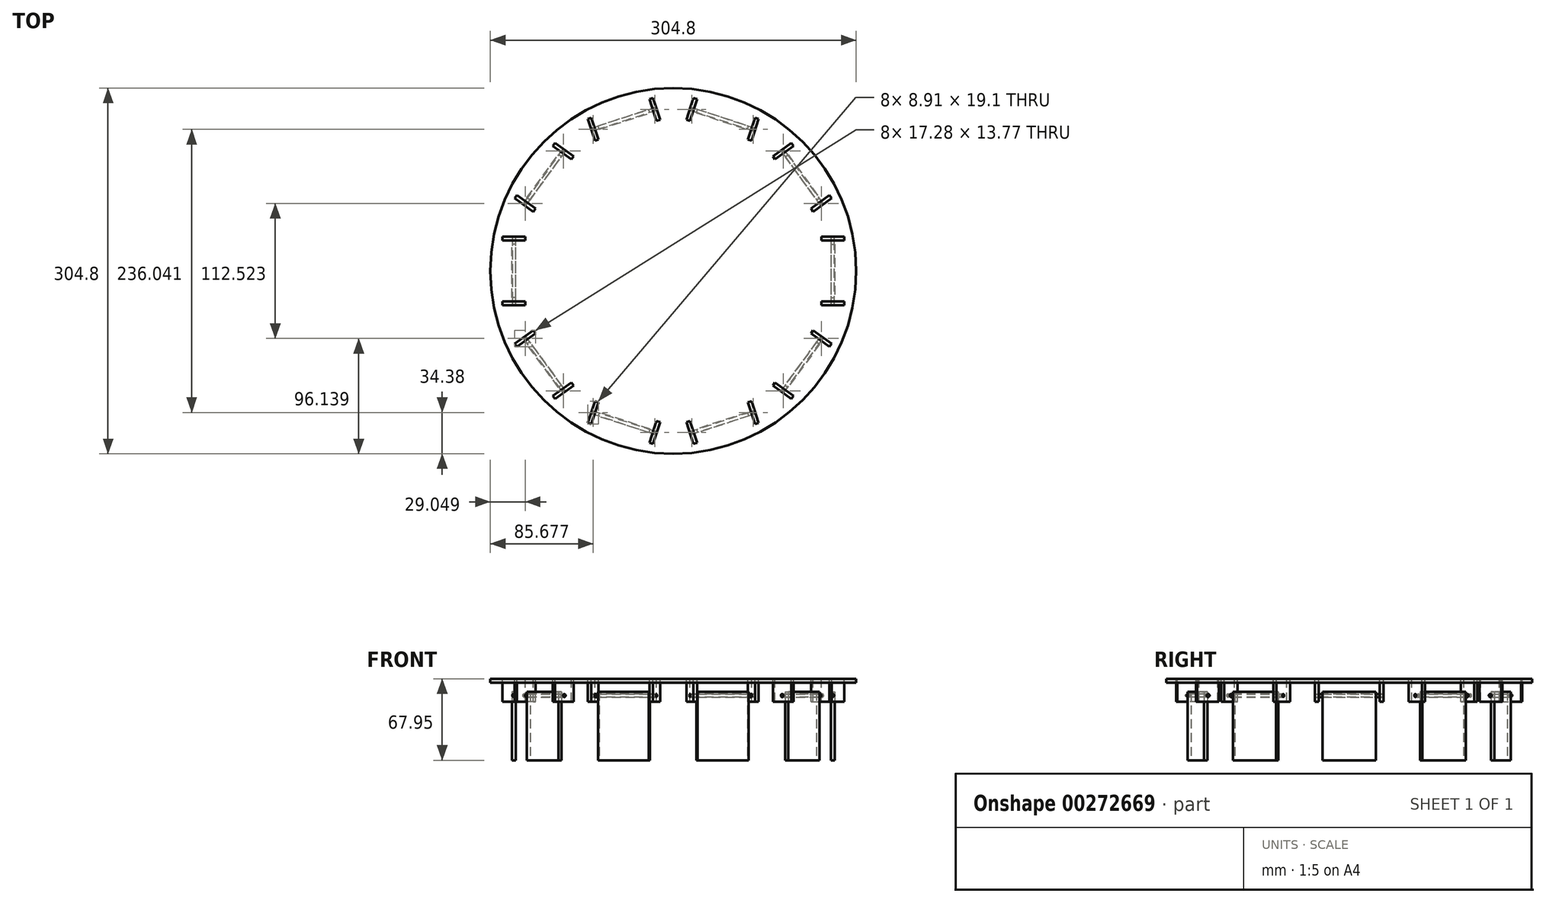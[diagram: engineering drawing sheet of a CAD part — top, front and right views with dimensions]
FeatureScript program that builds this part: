
annotation { "Feature Type Name" : "Feature", "Feature Type Description" : "" }
export const myFeature = defineFeature(function(context is Context, id is Id, definition is map)
    precondition{}
    {
        {
            var Q0;
            Q0=qCreatedBy(makeId("Top.planeOp"),FACE);
            var sketch = newSketch(context, id + "F0", { "sketchPlane" : qUnion([Q0])});
            skCircle(sketch, "E0", {"center": v(0, 0) * mm, "radius": 152.4 * mm});
            skSolve(sketch);
        }
        {
            var Q0;
            Q0 = qSketchRegion(id + "F0", true);
            extrude(context, id + "F1", {"entities" : qUnion([Q0]), "depth" : 3.17 * mm});
        }
        {
            var Q0;
            Q0=makeQuery(id+"F1.opExtrude","CAP_FACE",FACE,{"disambiguationData":[OSD([sQuery(id+"F0.wireOp",EDGE,"E0")])],"isStart":false});
            var sketch = newSketch(context, id + "F2", { "sketchPlane" : qUnion([Q0])});
            skLineSegment(sketch, "E1", {"start": v(0, 0) * mm, "end": v(0, 152.4) * mm, "construction": true});
            skLineSegment(sketch, "E2.1.0", {"start": v(0, 0) * mm, "end": v(-89.58, 123.3) * mm, "construction": true});
            skLineSegment(sketch, "E2.2.0", {"start": v(0, 0) * mm, "end": v(-144.94, 47.1) * mm, "construction": true});
            skLineSegment(sketch, "E2.3.0", {"start": v(0, 0) * mm, "end": v(-144.94, -47.1) * mm, "construction": true});
            skLineSegment(sketch, "E2.4.0", {"start": v(0, 0) * mm, "end": v(-89.58, -123.3) * mm, "construction": true});
            skLineSegment(sketch, "E2.5.0", {"start": v(0, 0) * mm, "end": v(0, -152.4) * mm, "construction": true});
            skLineSegment(sketch, "E2.6.0", {"start": v(0, 0) * mm, "end": v(89.58, -123.3) * mm, "construction": true});
            skLineSegment(sketch, "E2.7.0", {"start": v(0, 0) * mm, "end": v(144.94, -47.1) * mm, "construction": true});
            skLineSegment(sketch, "E2.8.0", {"start": v(0, 0) * mm, "end": v(144.94, 47.1) * mm, "construction": true});
            skLineSegment(sketch, "E2.9.0", {"start": v(0, 0) * mm, "end": v(89.58, 123.3) * mm, "construction": true});
            skPoint(sketch, "E2.center", {"position": v(0, 0) * mm});
            skLineSegment(sketch, "E3", {"start": v(0, 139.7) * mm, "end": v(82.11, 113.02) * mm, "construction": true});
            skLineSegment(sketch, "E4", {"start": v(16.23, 134.43) * mm, "end": v(66.72, 118.02) * mm, "construction": true});
            skLineSegment(sketch, "E5", {"start": v(41.06, 126.36) * mm, "end": v(0, 0) * mm, "construction": true});
            skLineSegment(sketch, "E6.bottom", {"start": v(65.29, 108.47) * mm, "end": v(62.27, 109.45) * mm});
            skLineSegment(sketch, "E6.top", {"start": v(71.18, 126.59) * mm, "end": v(68.16, 127.57) * mm});
            skLineSegment(sketch, "E6.left", {"start": v(65.29, 108.47) * mm, "end": v(71.18, 126.59) * mm});
            skLineSegment(sketch, "E6.right", {"start": v(62.27, 109.45) * mm, "end": v(68.16, 127.57) * mm});
            skPoint(sketch, "E6.middle", {"position": v(66.72, 118.02) * mm});
            skLineSegment(sketch, "E7.MirrorCS", {"start": v(13.96, 125.15) * mm, "end": v(19.84, 143.27) * mm});
            skLineSegment(sketch, "E8.MirrorCS", {"start": v(10.94, 126.13) * mm, "end": v(16.82, 144.25) * mm});
            skLineSegment(sketch, "E9.MirrorCS", {"start": v(10.94, 126.13) * mm, "end": v(13.96, 125.15) * mm});
            skLineSegment(sketch, "E10.MirrorCS", {"start": v(16.82, 144.25) * mm, "end": v(19.84, 143.27) * mm});
            skLineSegment(sketch, "E11.bottom", {"start": v(64.16, 125.53) * mm, "end": v(21.88, 139.27) * mm});
            skLineSegment(sketch, "E11.top", {"start": v(46.5, 71.18) * mm, "end": v(4.22, 84.91) * mm});
            skLineSegment(sketch, "E11.left", {"start": v(64.16, 125.53) * mm, "end": v(46.5, 71.18) * mm});
            skLineSegment(sketch, "E11.right", {"start": v(21.88, 139.27) * mm, "end": v(4.22, 84.91) * mm});
            skPoint(sketch, "E11.middle", {"position": v(34.19, 105.22) * mm});
            skSolve(sketch);
        }
        {
            var Q0;
            Q0=makeQuery(id+"F2.imprint","IMPRINT",FACE,{"disambiguationData":[TD([[makeQuery(id+"F2.imprint","IMPRINT",EDGE,{"derivedFrom":sQuery(id+"F2.wireOp",EDGE,"E7.MirrorCS")}),1.0]])]});
            var Q1;
            Q1=makeQuery(id+"F2.imprint","IMPRINT",FACE,{"disambiguationData":[TD([[makeQuery(id+"F2.imprint","IMPRINT",EDGE,{"derivedFrom":sQuery(id+"F2.wireOp",EDGE,"E6.bottom")}),-1.0]])]});
            extrude(context, id + "F3", {"entities" : qUnion([Q0, Q1]), "endBound" : BoundingType.UP_TO_NEXT, "oppositeDirection" : true, "depth" : 25.4 * mm});
        }
        {
            var Q0;
            Q0=makeQuery(id+"F3.opExtrude","SWEPT_BODY",BODY,{"disambiguationData":[OSD([sQuery(id+"F2.wireOp",EDGE,"E7.MirrorCS"),sQuery(id+"F2.wireOp",EDGE,"E8.MirrorCS"),sQuery(id+"F2.wireOp",EDGE,"E9.MirrorCS"),sQuery(id+"F2.wireOp",EDGE,"E10.MirrorCS")])]});
            var Q1;
            Q1=makeQuery(id+"F3.opExtrude","SWEPT_BODY",BODY,{"disambiguationData":[OSD([sQuery(id+"F2.wireOp",EDGE,"E6.bottom"),sQuery(id+"F2.wireOp",EDGE,"E6.top"),sQuery(id+"F2.wireOp",EDGE,"E6.left"),sQuery(id+"F2.wireOp",EDGE,"E6.right")])]});
            var Q2;
            Q2=makeQuery(id+"F1.opExtrude","CAP_EDGE",EDGE,{"disambiguationData":[OSD([sQuery(id+"F0.wireOp",EDGE,"E0")])],"isStart":false});
            circularPattern(context, id + "F4", {"entities" : qUnion([Q0, Q1]), "axis" : qUnion([Q2]), "angle" : 360 * degree, "instanceCount" : 10, "equalSpace" : true});
        }
        {
            var Q0;
            Q0=makeQuery(id+"F4.opPattern","COPY",BODY,{"derivedFrom":makeQuery(id+"F3.opExtrude","SWEPT_BODY",BODY,{"disambiguationData":[OSD([sQuery(id+"F2.wireOp",EDGE,"E7.MirrorCS"),sQuery(id+"F2.wireOp",EDGE,"E8.MirrorCS"),sQuery(id+"F2.wireOp",EDGE,"E9.MirrorCS"),sQuery(id+"F2.wireOp",EDGE,"E10.MirrorCS")])]}),"instanceName":"2"});
            var Q1;
            Q1=makeQuery(id+"F4.opPattern","COPY",BODY,{"derivedFrom":makeQuery(id+"F3.opExtrude","SWEPT_BODY",BODY,{"disambiguationData":[OSD([sQuery(id+"F2.wireOp",EDGE,"E6.bottom"),sQuery(id+"F2.wireOp",EDGE,"E6.top"),sQuery(id+"F2.wireOp",EDGE,"E6.left"),sQuery(id+"F2.wireOp",EDGE,"E6.right")])]}),"instanceName":"3"});
            var Q2;
            Q2=makeQuery(id+"F4.opPattern","COPY",BODY,{"derivedFrom":makeQuery(id+"F3.opExtrude","SWEPT_BODY",BODY,{"disambiguationData":[OSD([sQuery(id+"F2.wireOp",EDGE,"E7.MirrorCS"),sQuery(id+"F2.wireOp",EDGE,"E8.MirrorCS"),sQuery(id+"F2.wireOp",EDGE,"E9.MirrorCS"),sQuery(id+"F2.wireOp",EDGE,"E10.MirrorCS")])]}),"instanceName":"3"});
            var Q3;
            Q3=makeQuery(id+"F4.opPattern","COPY",BODY,{"derivedFrom":makeQuery(id+"F3.opExtrude","SWEPT_BODY",BODY,{"disambiguationData":[OSD([sQuery(id+"F2.wireOp",EDGE,"E6.bottom"),sQuery(id+"F2.wireOp",EDGE,"E6.top"),sQuery(id+"F2.wireOp",EDGE,"E6.left"),sQuery(id+"F2.wireOp",EDGE,"E6.right")])]}),"instanceName":"4"});
            var Q4;
            Q4=makeQuery(id+"F4.opPattern","COPY",BODY,{"derivedFrom":makeQuery(id+"F3.opExtrude","SWEPT_BODY",BODY,{"disambiguationData":[OSD([sQuery(id+"F2.wireOp",EDGE,"E7.MirrorCS"),sQuery(id+"F2.wireOp",EDGE,"E8.MirrorCS"),sQuery(id+"F2.wireOp",EDGE,"E9.MirrorCS"),sQuery(id+"F2.wireOp",EDGE,"E10.MirrorCS")])]}),"instanceName":"4"});
            var Q5;
            Q5=makeQuery(id+"F4.opPattern","COPY",BODY,{"derivedFrom":makeQuery(id+"F3.opExtrude","SWEPT_BODY",BODY,{"disambiguationData":[OSD([sQuery(id+"F2.wireOp",EDGE,"E6.bottom"),sQuery(id+"F2.wireOp",EDGE,"E6.top"),sQuery(id+"F2.wireOp",EDGE,"E6.left"),sQuery(id+"F2.wireOp",EDGE,"E6.right")])]}),"instanceName":"5"});
            var Q6;
            Q6=makeQuery(id+"F4.opPattern","COPY",BODY,{"derivedFrom":makeQuery(id+"F3.opExtrude","SWEPT_BODY",BODY,{"disambiguationData":[OSD([sQuery(id+"F2.wireOp",EDGE,"E7.MirrorCS"),sQuery(id+"F2.wireOp",EDGE,"E8.MirrorCS"),sQuery(id+"F2.wireOp",EDGE,"E9.MirrorCS"),sQuery(id+"F2.wireOp",EDGE,"E10.MirrorCS")])]}),"instanceName":"5"});
            var Q7;
            Q7=makeQuery(id+"F4.opPattern","COPY",BODY,{"derivedFrom":makeQuery(id+"F3.opExtrude","SWEPT_BODY",BODY,{"disambiguationData":[OSD([sQuery(id+"F2.wireOp",EDGE,"E6.bottom"),sQuery(id+"F2.wireOp",EDGE,"E6.top"),sQuery(id+"F2.wireOp",EDGE,"E6.left"),sQuery(id+"F2.wireOp",EDGE,"E6.right")])]}),"instanceName":"6"});
            var Q8;
            Q8=makeQuery(id+"F4.opPattern","COPY",BODY,{"derivedFrom":makeQuery(id+"F3.opExtrude","SWEPT_BODY",BODY,{"disambiguationData":[OSD([sQuery(id+"F2.wireOp",EDGE,"E7.MirrorCS"),sQuery(id+"F2.wireOp",EDGE,"E8.MirrorCS"),sQuery(id+"F2.wireOp",EDGE,"E9.MirrorCS"),sQuery(id+"F2.wireOp",EDGE,"E10.MirrorCS")])]}),"instanceName":"6"});
            var Q9;
            Q9=makeQuery(id+"F4.opPattern","COPY",BODY,{"derivedFrom":makeQuery(id+"F3.opExtrude","SWEPT_BODY",BODY,{"disambiguationData":[OSD([sQuery(id+"F2.wireOp",EDGE,"E6.bottom"),sQuery(id+"F2.wireOp",EDGE,"E6.top"),sQuery(id+"F2.wireOp",EDGE,"E6.left"),sQuery(id+"F2.wireOp",EDGE,"E6.right")])]}),"instanceName":"7"});
            var Q10;
            Q10=makeQuery(id+"F4.opPattern","COPY",BODY,{"derivedFrom":makeQuery(id+"F3.opExtrude","SWEPT_BODY",BODY,{"disambiguationData":[OSD([sQuery(id+"F2.wireOp",EDGE,"E7.MirrorCS"),sQuery(id+"F2.wireOp",EDGE,"E8.MirrorCS"),sQuery(id+"F2.wireOp",EDGE,"E9.MirrorCS"),sQuery(id+"F2.wireOp",EDGE,"E10.MirrorCS")])]}),"instanceName":"7"});
            var Q11;
            Q11=makeQuery(id+"F4.opPattern","COPY",BODY,{"derivedFrom":makeQuery(id+"F3.opExtrude","SWEPT_BODY",BODY,{"disambiguationData":[OSD([sQuery(id+"F2.wireOp",EDGE,"E6.bottom"),sQuery(id+"F2.wireOp",EDGE,"E6.top"),sQuery(id+"F2.wireOp",EDGE,"E6.left"),sQuery(id+"F2.wireOp",EDGE,"E6.right")])]}),"instanceName":"8"});
            var Q12;
            Q12=makeQuery(id+"F4.opPattern","COPY",BODY,{"derivedFrom":makeQuery(id+"F3.opExtrude","SWEPT_BODY",BODY,{"disambiguationData":[OSD([sQuery(id+"F2.wireOp",EDGE,"E7.MirrorCS"),sQuery(id+"F2.wireOp",EDGE,"E8.MirrorCS"),sQuery(id+"F2.wireOp",EDGE,"E9.MirrorCS"),sQuery(id+"F2.wireOp",EDGE,"E10.MirrorCS")])]}),"instanceName":"8"});
            var Q13;
            Q13=makeQuery(id+"F4.opPattern","COPY",BODY,{"derivedFrom":makeQuery(id+"F3.opExtrude","SWEPT_BODY",BODY,{"disambiguationData":[OSD([sQuery(id+"F2.wireOp",EDGE,"E6.bottom"),sQuery(id+"F2.wireOp",EDGE,"E6.top"),sQuery(id+"F2.wireOp",EDGE,"E6.left"),sQuery(id+"F2.wireOp",EDGE,"E6.right")])]}),"instanceName":"9"});
            var Q14;
            Q14=makeQuery(id+"F4.opPattern","COPY",BODY,{"derivedFrom":makeQuery(id+"F3.opExtrude","SWEPT_BODY",BODY,{"disambiguationData":[OSD([sQuery(id+"F2.wireOp",EDGE,"E7.MirrorCS"),sQuery(id+"F2.wireOp",EDGE,"E8.MirrorCS"),sQuery(id+"F2.wireOp",EDGE,"E9.MirrorCS"),sQuery(id+"F2.wireOp",EDGE,"E10.MirrorCS")])]}),"instanceName":"9"});
            var Q15;
            Q15=makeQuery(id+"F3.opExtrude","SWEPT_BODY",BODY,{"disambiguationData":[OSD([sQuery(id+"F2.wireOp",EDGE,"E6.bottom"),sQuery(id+"F2.wireOp",EDGE,"E6.top"),sQuery(id+"F2.wireOp",EDGE,"E6.left"),sQuery(id+"F2.wireOp",EDGE,"E6.right")])]});
            var Q16;
            Q16=makeQuery(id+"F3.opExtrude","SWEPT_BODY",BODY,{"disambiguationData":[OSD([sQuery(id+"F2.wireOp",EDGE,"E7.MirrorCS"),sQuery(id+"F2.wireOp",EDGE,"E8.MirrorCS"),sQuery(id+"F2.wireOp",EDGE,"E9.MirrorCS"),sQuery(id+"F2.wireOp",EDGE,"E10.MirrorCS")])]});
            var Q17;
            Q17=makeQuery(id+"F4.opPattern","COPY",BODY,{"derivedFrom":makeQuery(id+"F3.opExtrude","SWEPT_BODY",BODY,{"disambiguationData":[OSD([sQuery(id+"F2.wireOp",EDGE,"E6.bottom"),sQuery(id+"F2.wireOp",EDGE,"E6.top"),sQuery(id+"F2.wireOp",EDGE,"E6.left"),sQuery(id+"F2.wireOp",EDGE,"E6.right")])]}),"instanceName":"1"});
            var Q18;
            Q18=makeQuery(id+"F4.opPattern","COPY",BODY,{"derivedFrom":makeQuery(id+"F3.opExtrude","SWEPT_BODY",BODY,{"disambiguationData":[OSD([sQuery(id+"F2.wireOp",EDGE,"E7.MirrorCS"),sQuery(id+"F2.wireOp",EDGE,"E8.MirrorCS"),sQuery(id+"F2.wireOp",EDGE,"E9.MirrorCS"),sQuery(id+"F2.wireOp",EDGE,"E10.MirrorCS")])]}),"instanceName":"1"});
            var Q19;
            Q19=makeQuery(id+"F4.opPattern","COPY",BODY,{"derivedFrom":makeQuery(id+"F3.opExtrude","SWEPT_BODY",BODY,{"disambiguationData":[OSD([sQuery(id+"F2.wireOp",EDGE,"E6.bottom"),sQuery(id+"F2.wireOp",EDGE,"E6.top"),sQuery(id+"F2.wireOp",EDGE,"E6.left"),sQuery(id+"F2.wireOp",EDGE,"E6.right")])]}),"instanceName":"2"});
            var Q20;
            Q20=makeQuery(id+"F1.opExtrude","SWEPT_BODY",BODY,{"disambiguationData":[OSD([sQuery(id+"F0.wireOp",EDGE,"E0")])]});
            booleanBodies(context, id + "F5", {"operationType" : BooleanOperationType.SUBTRACTION, "tools" : qUnion([Q0, Q1, Q2, Q3, Q4, Q5, Q6, Q7, Q8, Q9, Q10, Q11, Q12, Q13, Q14, Q15, Q16, Q17, Q18, Q19]), "targets" : qUnion([Q20])});
        }
        {
            var Q0;
            Q0=makeQuery(id+"F1.opExtrude","CAP_FACE",FACE,{"disambiguationData":[OSD([sQuery(id+"F0.wireOp",EDGE,"E0")])],"isStart":false});
            var sketch = newSketch(context, id + "F6", { "sketchPlane" : qUnion([Q0])});
            skLineSegment(sketch, "E12.0", {"start": v(10.94, 126.13) * mm, "end": v(16.82, 144.25) * mm});
            skLineSegment(sketch, "E13.0", {"start": v(13.96, 125.15) * mm, "end": v(19.84, 143.27) * mm});
            skLineSegment(sketch, "E14.0", {"start": v(16.82, 144.25) * mm, "end": v(19.84, 143.27) * mm});
            skLineSegment(sketch, "E15.0", {"start": v(10.94, 126.13) * mm, "end": v(13.96, 125.15) * mm});
            skLineSegment(sketch, "E16.0", {"start": v(71.18, 126.59) * mm, "end": v(68.16, 127.57) * mm});
            skLineSegment(sketch, "E17.0", {"start": v(62.27, 109.45) * mm, "end": v(68.16, 127.57) * mm});
            skLineSegment(sketch, "E18.0", {"start": v(65.29, 108.47) * mm, "end": v(71.18, 126.59) * mm});
            skLineSegment(sketch, "E19.0", {"start": v(65.29, 108.47) * mm, "end": v(62.27, 109.45) * mm});
            skSolve(sketch);
        }
        {
            var Q0;
            Q0 = qSketchRegion(id + "F6", true);
            extrude(context, id + "F7", {"entities" : qUnion([Q0]), "oppositeDirection" : true, "depth" : 19.05 * mm});
        }
        {
            var Q0;
            Q0=makeQuery(id+"F7.opExtrude","SWEPT_FACE",FACE,{"disambiguationData":[OSD([sQuery(id+"F6.wireOp",EDGE,"E12.0")])]});
            var sketch = newSketch(context, id + "F8", { "sketchPlane" : qUnion([Q0])});
            skCircle(sketch, "E20", {"center": v(-132.86, -10.8) * mm, "radius": 1.27 * mm});
            skPoint(sketch, "E20.centerSnap0", {"position": v(-132.86, -15.88) * mm});
            skSolve(sketch);
        }
        {
            var Q0;
            Q0 = qSketchRegion(id + "F8", true);
            extrude(context, id + "F9", {"entities" : qUnion([Q0]), "operationType" : NewBodyOperationType.REMOVE, "endBound" : BoundingType.THROUGH_ALL, "oppositeDirection" : true, "depth" : 25.4 * mm});
        }
        {
            var Q0;
            Q0=makeQuery(id+"F7.opExtrude","SWEPT_FACE",FACE,{"disambiguationData":[OSD([sQuery(id+"F6.wireOp",EDGE,"E12.0")])]});
            var sketch = newSketch(context, id + "F10", { "sketchPlane" : qUnion([Q0])});
            skCircle(sketch, "E21.0", {"center": v(-132.86, -10.8) * mm, "radius": 1.27 * mm});
            skSolve(sketch);
        }
        {
            var Q0;
            Q0 = qSketchRegion(id + "F10", true);
            var Q1;
            Q1=makeQuery(id+"F7.opExtrude","SWEPT_FACE",FACE,{"disambiguationData":[OSD([sQuery(id+"F6.wireOp",EDGE,"E18.0")])]});
            extrude(context, id + "F11", {"entities" : qUnion([Q0]), "endBound" : BoundingType.UP_TO_SURFACE, "oppositeDirection" : true, "endBoundEntityFace" : qUnion([Q1]), "depth" : 25.4 * mm});
        }
        {
            var Q0;
            Q0=makeQuery(id+"F7.opExtrude","SWEPT_FACE",FACE,{"disambiguationData":[OSD([sQuery(id+"F6.wireOp",EDGE,"E12.0")])]});
            var Q1;
            Q1=makeQuery(id+"F7.opExtrude","SWEPT_FACE",FACE,{"disambiguationData":[OSD([sQuery(id+"F6.wireOp",EDGE,"E18.0")])]});
            cPlane(context, id + "F12", {"entities" : qUnion([Q0, Q1]), "cplaneType" : CPlaneType.MID_PLANE, "offset" : 25.4 * mm, "width" : 152.4 * mm, "height" : 152.4 * mm});
        }
        {
            var Q0;
            Q0=qCreatedBy(id+"F12.planeOp",FACE);
            var sketch = newSketch(context, id + "F13", { "sketchPlane" : qUnion([Q0])});
            skCircle(sketch, "E22.0", {"center": v(-132.86, -10.8) * mm, "radius": 1.27 * mm, "construction": true});
            skLineSegment(sketch, "E23", {"start": v(-132.86, -10.8) * mm, "end": v(-132.86, -59.9) * mm, "construction": true});
            skLineSegment(sketch, "E24.bottom", {"start": v(-131.28, -7.62) * mm, "end": v(-134.45, -7.62) * mm});
            skLineSegment(sketch, "E24.top", {"start": v(-131.28, -64.77) * mm, "end": v(-134.45, -64.77) * mm});
            skLineSegment(sketch, "E24.left", {"start": v(-131.28, -7.62) * mm, "end": v(-131.28, -64.77) * mm});
            skLineSegment(sketch, "E24.right", {"start": v(-134.45, -7.62) * mm, "end": v(-134.45, -64.77) * mm});
            skPoint(sketch, "E24.middle", {"position": v(-132.86, -36.2) * mm});
            skSolve(sketch);
        }
        {
            var Q0;
            Q0 = qSketchRegion(id + "F13", true);
            extrude(context, id + "F14", {"entities" : qUnion([Q0]), "endBound" : BoundingType.SYMMETRIC, "depth" : 44.45 * mm});
        }
        {
            var Q0;
            Q0=makeQuery(id+"F7.opExtrude","SWEPT_BODY",BODY,{"disambiguationData":[OSD([sQuery(id+"F6.wireOp",EDGE,"E16.0"),sQuery(id+"F6.wireOp",EDGE,"E17.0"),sQuery(id+"F6.wireOp",EDGE,"E18.0"),sQuery(id+"F6.wireOp",EDGE,"E19.0")])]});
            var Q1;
            Q1=makeQuery(id+"F7.opExtrude","SWEPT_BODY",BODY,{"disambiguationData":[OSD([sQuery(id+"F6.wireOp",EDGE,"E12.0"),sQuery(id+"F6.wireOp",EDGE,"E13.0"),sQuery(id+"F6.wireOp",EDGE,"E14.0"),sQuery(id+"F6.wireOp",EDGE,"E15.0")])]});
            var Q2;
            Q2=makeQuery(id+"F14.opExtrude","SWEPT_BODY",BODY,{"disambiguationData":[OSD([sQuery(id+"F13.wireOp",EDGE,"E24.bottom"),sQuery(id+"F13.wireOp",EDGE,"E24.top"),sQuery(id+"F13.wireOp",EDGE,"E24.left"),sQuery(id+"F13.wireOp",EDGE,"E24.right")])]});
            var Q3;
            Q3=makeQuery(id+"F11.opExtrude","SWEPT_BODY",BODY,{"disambiguationData":[OSD([sQuery(id+"F10.wireOp",EDGE,"E21.0")])]});
            var Q4;
            Q4=makeQuery(id+"F1.opExtrude","CAP_EDGE",EDGE,{"disambiguationData":[OSD([sQuery(id+"F0.wireOp",EDGE,"E0")])],"isStart":true});
            circularPattern(context, id + "F15", {"entities" : qUnion([Q0, Q1, Q2, Q3]), "axis" : qUnion([Q4]), "angle" : 360 * degree, "instanceCount" : 10, "equalSpace" : true});
        }
    });
